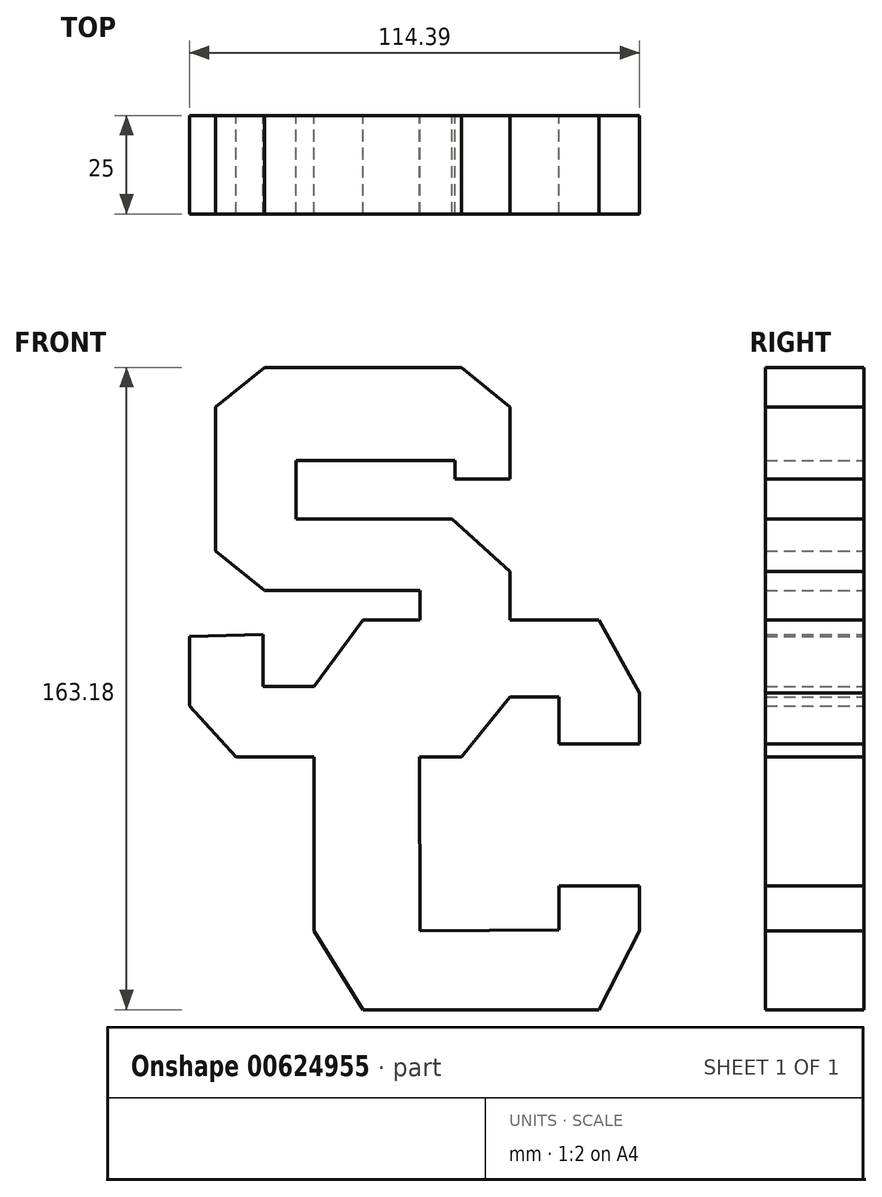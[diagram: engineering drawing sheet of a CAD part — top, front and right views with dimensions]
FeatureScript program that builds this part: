
annotation { "Feature Type Name" : "Feature", "Feature Type Description" : "" }
export const myFeature = defineFeature(function(context is Context, id is Id, definition is map)
    precondition{}
    {
        {
            var Q0;
            Q0=qCreatedBy(makeId("Front.planeOp"),FACE);
            var sketch = newSketch(context, id + "F0", { "sketchPlane" : qUnion([Q0])});
            skLineSegment(sketch, "E0", {"start": v(-25, 54.4) * mm, "end": v(25, 54.4) * mm});
            skLineSegment(sketch, "E1", {"start": v(25, 54.4) * mm, "end": v(37.4, 44.28) * mm});
            skLineSegment(sketch, "E2.MirrorCS", {"start": v(-25, 54.4) * mm, "end": v(-37.4, 44.28) * mm});
            skLineSegment(sketch, "E3", {"start": v(-37.4, 44.28) * mm, "end": v(-37.4, 7.76) * mm});
            skLineSegment(sketch, "E4", {"start": v(-37.4, 7.76) * mm, "end": v(-25, -2.35) * mm});
            skLineSegment(sketch, "E5", {"start": v(37.4, 44.28) * mm, "end": v(37.4, 26.04) * mm});
            skLineSegment(sketch, "E6", {"start": v(37.4, 26.04) * mm, "end": v(23.42, 26.04) * mm});
            skLineSegment(sketch, "E7", {"start": v(23.42, 26.04) * mm, "end": v(23.42, 30.78) * mm});
            skLineSegment(sketch, "E8", {"start": v(23.42, 30.78) * mm, "end": v(-17, 30.78) * mm});
            skLineSegment(sketch, "E9", {"start": v(-17, 30.78) * mm, "end": v(-17, 15.9) * mm});
            skLineSegment(sketch, "E10", {"start": v(-17, 15.9) * mm, "end": v(22.65, 15.9) * mm});
            skLineSegment(sketch, "E11", {"start": v(22.65, 15.9) * mm, "end": v(37.4, 2.5) * mm});
            skLineSegment(sketch, "E12", {"start": v(37.4, 2.5) * mm, "end": v(37.4, -29.37) * mm});
            skLineSegment(sketch, "E13", {"start": v(-25, -2.35) * mm, "end": v(14.55, -2.35) * mm});
            skLineSegment(sketch, "E14", {"start": v(14.55, -2.35) * mm, "end": v(14.55, -26.7) * mm});
            skLineSegment(sketch, "E15", {"start": v(37.4, -29.37) * mm, "end": v(25, -44.58) * mm});
            skLineSegment(sketch, "E16", {"start": v(25, -44.58) * mm, "end": v(-32.25, -44.58) * mm});
            skLineSegment(sketch, "E17", {"start": v(-25.36, -13.52) * mm, "end": v(-25.36, -26.7) * mm});
            skLineSegment(sketch, "E18", {"start": v(-25.36, -26.7) * mm, "end": v(14.55, -26.7) * mm});
            skLineSegment(sketch, "E19", {"start": v(-32.25, -44.58) * mm, "end": v(-44.09, -31.58) * mm});
            skLineSegment(sketch, "E20", {"start": v(-44.09, -31.58) * mm, "end": v(-44.09, -14.03) * mm});
            skLineSegment(sketch, "E21", {"start": v(-44.09, -14.03) * mm, "end": v(-25.36, -13.52) * mm});
            skLineSegment(sketch, "E22", {"start": v(-12.42, -26.7) * mm, "end": v(0, -9.74) * mm});
            skLineSegment(sketch, "E23", {"start": v(0, -9.74) * mm, "end": v(59.96, -9.74) * mm});
            skLineSegment(sketch, "E24", {"start": v(59.96, -9.74) * mm, "end": v(70.3, -28.27) * mm});
            skLineSegment(sketch, "E25", {"start": v(70.3, -28.27) * mm, "end": v(70.3, -41.21) * mm});
            skLineSegment(sketch, "E26", {"start": v(70.3, -41.21) * mm, "end": v(49.8, -41.21) * mm});
            skLineSegment(sketch, "E27", {"start": v(49.8, -41.21) * mm, "end": v(49.8, -29.37) * mm});
            skLineSegment(sketch, "E28", {"start": v(49.8, -29.37) * mm, "end": v(37.4, -29.37) * mm});
            skLineSegment(sketch, "E29", {"start": v(-12.42, -44.58) * mm, "end": v(-12.42, -88.71) * mm});
            skLineSegment(sketch, "E30", {"start": v(-12.42, -88.71) * mm, "end": v(0, -108.8) * mm});
            skLineSegment(sketch, "E31", {"start": v(0, -108.8) * mm, "end": v(59.96, -108.8) * mm});
            skLineSegment(sketch, "E32", {"start": v(59.96, -108.8) * mm, "end": v(70.3, -88.71) * mm});
            skLineSegment(sketch, "E33", {"start": v(70.3, -88.71) * mm, "end": v(70.3, -77.31) * mm});
            skLineSegment(sketch, "E34", {"start": v(70.3, -77.31) * mm, "end": v(49.8, -77.31) * mm});
            skLineSegment(sketch, "E35", {"start": v(49.8, -77.31) * mm, "end": v(49.8, -88.56) * mm});
            skLineSegment(sketch, "E36", {"start": v(14.55, -88.71) * mm, "end": v(49.8, -88.56) * mm});
            skLineSegment(sketch, "E37", {"start": v(14.55, -88.71) * mm, "end": v(14.36, -44.58) * mm});
            skSolve(sketch);
        }
        {
            var Q0;
            Q0 = qSketchRegion(id + "F0", true);
            extrude(context, id + "F1", {"entities" : qUnion([Q0]), "depth" : 25 * mm, "offsetDistance" : 25 * mm});
        }
    });
